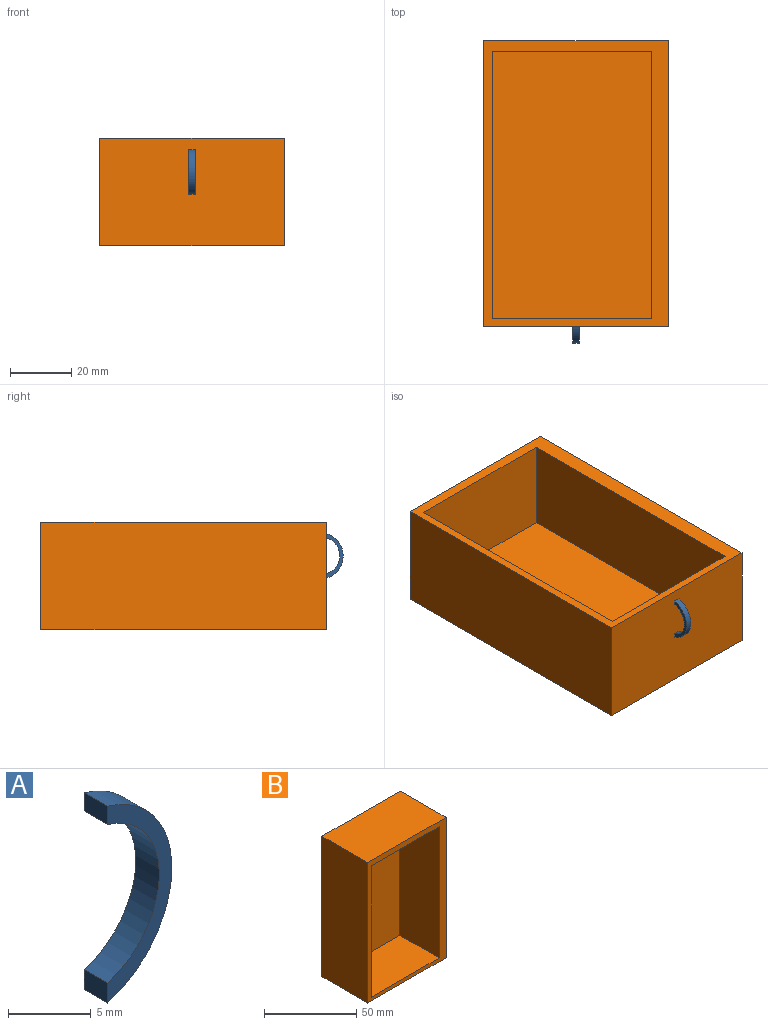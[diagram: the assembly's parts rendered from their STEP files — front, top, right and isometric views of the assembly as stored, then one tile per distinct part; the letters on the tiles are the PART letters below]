
ASSEMBLY  parts=2 mates=1
PART A: 6 faces, bbox 5.5x2x14.5 mm
  f0: cylinder r=7.56mm len=14.53mm, axis (0,1,0), area 39mm2, adj f1,f3,f4,f5
  f1: plane 2x1.35mm, normal (-1,0,0), area 2.7mm2, adj f0,f2,f4,f5
  f2: cylinder r=6.1mm len=11.72mm, axis (0,1,0), area 31.4mm2, adj f1,f3,f4,f5
  f3: plane 2x1.47mm, normal (-1,0,0), area 2.9mm2, adj f0,f2,f4,f5
  f4: plane 14.53x5.47mm, normal (0,-1,0), area 20.7mm2, adj f0,f1,f2,f3
  f5: plane 14.53x5.47mm, normal (0,1,0), area 20.7mm2, adj f0,f1,f2,f3
PART B: 11 faces, bbox 60x35x93 mm
  f0: plane 93x60mm, normal (0,-1,0), area 1056mm2, adj f2,f3,f4,f5,f6,f7,f8,f9
  f1: plane 93x60mm, normal (0,1,0), area 5580mm2, adj f2,f3,f4,f5
  f2: plane 93x35mm, normal (-1,0,0), area 3255mm2, adj f0,f1,f4,f5
  f3: plane 93x35mm, normal (1,0,0), area 3255mm2, adj f0,f1,f4,f5
  f4: plane 60x35mm, normal (0,0,1), area 2100mm2, adj f0,f1,f2,f3
  f5: plane 60x35mm, normal (0,0,-1), area 2100mm2, adj f0,f1,f2,f3
  f6: plane 52x30mm, normal (0,0,-1), area 1560mm2, adj f0,f7,f9,f10
  f7: plane 87x30mm, normal (1,0,0), area 2610mm2, adj f0,f6,f8,f10
  f8: plane 52x30mm, normal (0,0,1), area 1560mm2, adj f0,f7,f9,f10
  f9: plane 87x30mm, normal (-1,0,0), area 2610mm2, adj f0,f6,f8,f10
  f10: plane 87x52mm, normal (0,-1,0), area 4524mm2, adj f6,f7,f8,f9
PLACE A rot(axis=(0,0,-1),90deg) t=(18.68,54.87,123.62)mm
PLACE B rot(axis=(-1,0,0),90deg) t=(15.57,54.87,120.42)mm
MATE fastened A.f3 <-> B.f5  axis (0,1,0) through (17.68,54.87,118.42)mm
